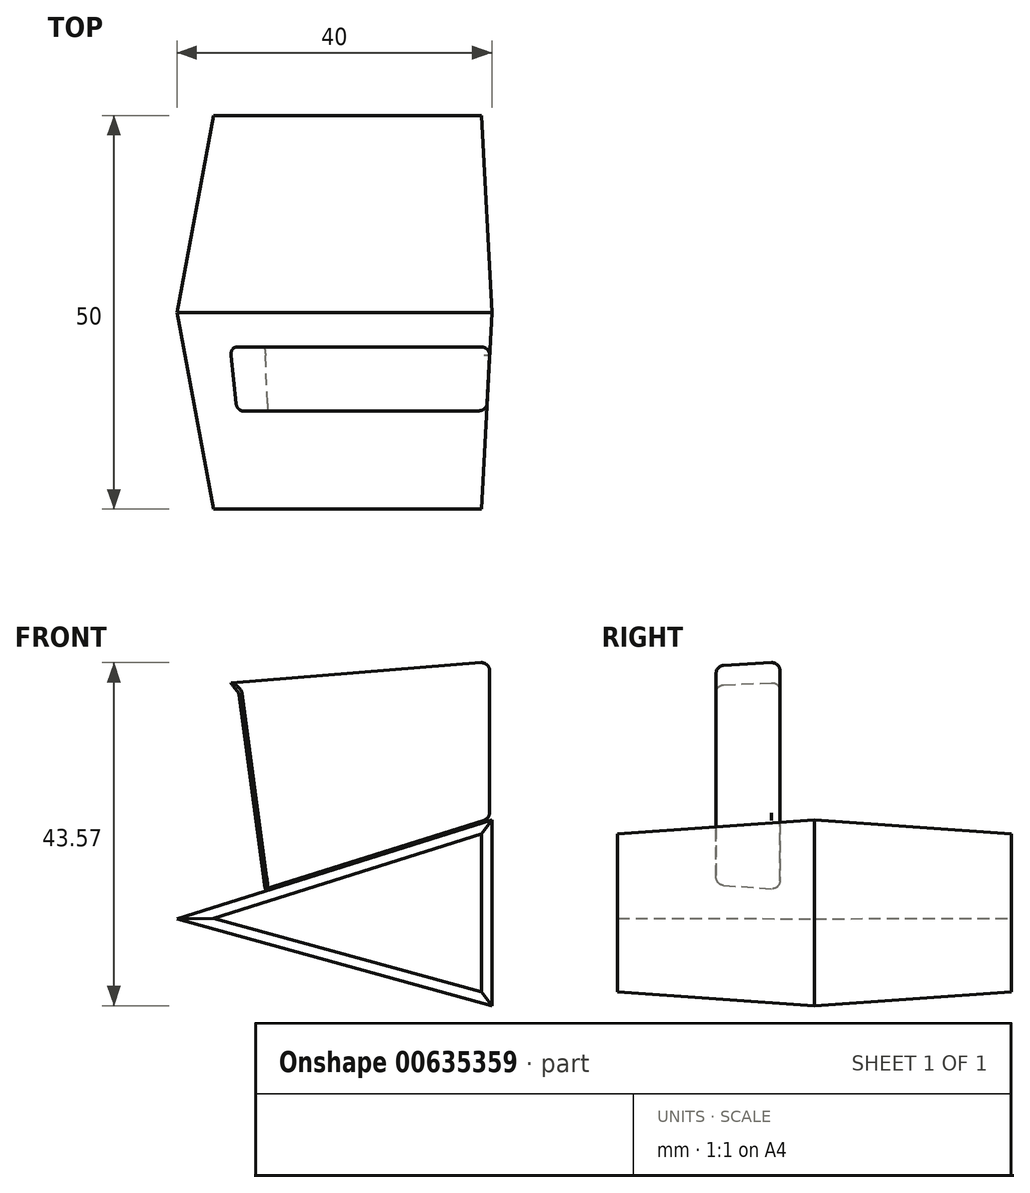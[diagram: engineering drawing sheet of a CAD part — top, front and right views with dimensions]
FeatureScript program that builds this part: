
annotation { "Feature Type Name" : "Feature", "Feature Type Description" : "" }
export const myFeature = defineFeature(function(context is Context, id is Id, definition is map)
    precondition{}
    {
        {
            var Q0;
            Q0=qCreatedBy(makeId("Front.planeOp"),FACE);
            var sketch = newSketch(context, id + "F0", { "sketchPlane" : qUnion([Q0])});
            skLineSegment(sketch, "E0", {"start": v(-45.52, 27.28) * mm, "end": v(-40.7, 21.55) * mm});
            skLineSegment(sketch, "E1", {"start": v(-40.7, 21.55) * mm, "end": v(-33.18, -34.43) * mm});
            skLineSegment(sketch, "E2", {"start": v(-33.18, -34.43) * mm, "end": v(-8.32, -34.43) * mm});
            skLineSegment(sketch, "E3", {"start": v(-8.32, -34.43) * mm, "end": v(-8.32, 25.85) * mm});
            skLineSegment(sketch, "E4", {"start": v(-8.32, 25.85) * mm, "end": v(-61.62, 21.55) * mm});
            skLineSegment(sketch, "E5", {"start": v(-48.32, -7.08) * mm, "end": v(1.47, 8.52) * mm});
            skLineSegment(sketch, "E6", {"start": v(0, -20.41) * mm, "end": v(-48.32, -7.08) * mm});
            skSolve(sketch);
        }
        {
            var Q0;
            {var subQ0=sQuery(id+"F0.wireOp",EDGE,"E5");var subQ1=sQuery(id+"F0.wireOp",EDGE,"E1");var subQ2=makeQuery(id+"F0.imprint","INTERSECT",VERTEX,{"derivedFrom":[subQ1,subQ0]});Q0=makeQuery(id+"F0.imprint","IMPRINT",FACE,{"disambiguationData":[TD([[makeQuery(id+"F0.imprint","IMPRINT",EDGE,{"disambiguationData":[TD([[subQ2,-1.0]])],"derivedFrom":subQ1}),-1.0]])]});}
            var Q1;
            {var subQ0=sQuery(id+"F0.wireOp",EDGE,"E5");var subQ1=sQuery(id+"F0.wireOp",EDGE,"E1");var subQ2=makeQuery(id+"F0.imprint","INTERSECT",VERTEX,{"derivedFrom":[subQ1,subQ0]});Q1=makeQuery(id+"F0.imprint","IMPRINT",FACE,{"disambiguationData":[TD([[makeQuery(id+"F0.imprint","IMPRINT",EDGE,{"disambiguationData":[TD([[subQ2,-1.0]])],"derivedFrom":subQ1}),1.0]])]});}
            extrude(context, id + "F1", {"entities" : qUnion([Q0, Q1]), "depth" : 25 * mm, "offsetDistance" : 25 * mm, "hasDraft" : true, "draftAngle" : 3 * degree, "draftPullDirection" : true, "hasSecondDirection" : true, "secondDirectionOppositeDirection" : true, "secondDirectionDepth" : 25 * mm, "hasSecondDirectionDraft" : true, "secondDirectionDraftAngle" : 3 * degree, "secondDirectionDraftPullDirection" : true});
        }
        {
            var Q0;
            {var subQ3=sQuery(id+"F0.wireOp",EDGE,"E0");var subQ7=sQuery(id+"F0.wireOp",EDGE,"E1");var subQ8=makeQuery(id+"F0.imprint","INTERSECT",VERTEX,{"derivedFrom":[subQ3,subQ7]});Q0=makeQuery(id+"F0.imprint","IMPRINT",FACE,{"disambiguationData":[TD([[makeQuery(id+"F0.imprint","IMPRINT",EDGE,{"disambiguationData":[TD([[subQ8,1.0]])],"derivedFrom":subQ3}),1.0]])]});}
            extrude(context, id + "F2", {"entities" : qUnion([Q0]), "depth" : 12.5 * mm, "offsetDistance" : 25 * mm, "hasDraft" : true, "draftAngle" : 3 * degree, "draftPullDirection" : true, "hasSecondDirection" : true, "secondDirectionOppositeDirection" : false, "secondDirectionDepth" : 4.4 * mm});
        }
        {
            var Q0;
            Q0=makeQuery(id+"F2.opExtrude","SWEPT_FACE",FACE,{"disambiguationData":[OSD([sQuery(id+"F0.wireOp",EDGE,"E3")])]});
            var Q1;
            Q1=makeQuery(id+"F2.opExtrude","CAP_EDGE",EDGE,{"disambiguationData":[OSD([sQuery(id+"F0.wireOp",EDGE,"E4")])],"isStart":false});
            var Q2;
            Q2=makeQuery(id+"F2.opExtrude","CAP_EDGE",EDGE,{"disambiguationData":[OSD([sQuery(id+"F0.wireOp",EDGE,"E5")])],"isStart":false});
            var Q3;
            Q3=makeQuery(id+"F2.opExtrude","CAP_EDGE",EDGE,{"disambiguationData":[OSD([sQuery(id+"F0.wireOp",EDGE,"E4")])],"isStart":true});
            var Q4;
            Q4=makeQuery(id+"F2.opExtrude","CAP_EDGE",EDGE,{"disambiguationData":[OSD([sQuery(id+"F0.wireOp",EDGE,"E5")])],"isStart":true});
            var Q5;
            Q5=makeQuery(id+"F2.opExtrude","SWEPT_EDGE",EDGE,{"disambiguationData":[OSD([sQuery(id+"F0.wireOp",EDGE,"E0"),sQuery(id+"F0.wireOp",EDGE,"E1")])]});
            fillet(context, id + "F3", {"entities" : qUnion([Q0, Q1, Q2, Q3, Q4, Q5]), "radius" : 1 * mm, "tangentPropagation" : true, "allowEdgeOverflow" : false});
        }
    });
